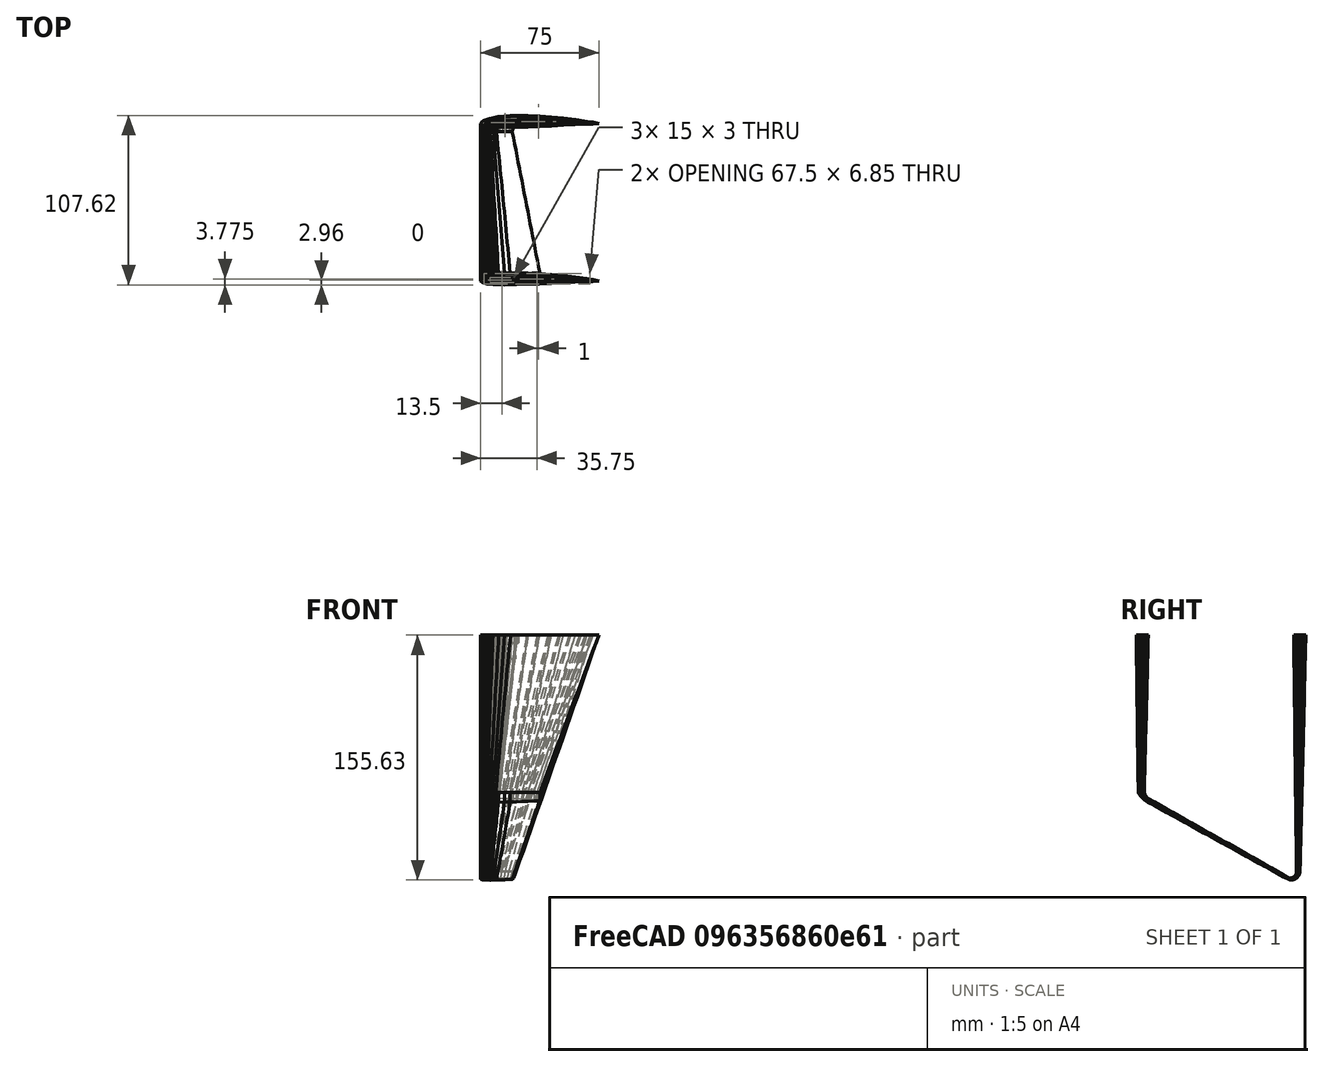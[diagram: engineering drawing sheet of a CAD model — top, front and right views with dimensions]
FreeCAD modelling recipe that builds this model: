
FCSTD DOCUMENT  (FreeCAD 0.16R6712 (Git))
Label: Aile_double_tribord_2
License: All rights reserved
LicenseURL: http://en.wikipedia.org/wiki/All_rights_reserved
objects: Part::FeaturePython×6, Part::Loft×5, Part::Part2DObjectPython×4, Sketcher::SketchObject×3, Part::Sweep×2, Part::Cut×2, PartDesign::Pad×2, Mesh::Feature×2, Part::MultiFuse×1
note: 27 computed .brp shape members not serialized (recipe doc carries the construction recipe); baked Part::Feature solids carry a one-line shape summary decoded from their .brp

FEATURE [Part::Part2DObjectPython] DWire  label="DWire_base"  # Draft 2D object (typed FeaturePython)
  ChamferSize = 0
  Closed = true
  End = (75,-0.07875,0)
  FilletRadius = 0
  Length = 152.352
  MakeFace = true
  Points = (35) [(75,0.07875,0),(71.2807,0.7425,0),(67.5502,1.362,0),(60.0727,2.472,0),(52.5765,3.41325,0),(45.0637,4.185,0),(37.5367,4.767,0),(30,5.12775,0),+27 more]
  Start = (75,0.07875,0)
  Subdivisions = 0
FEATURE [Part::FeaturePython] Scale  label="Scale_bout"  # Draft clone (typed FeaturePython)
  Objects = -> [DWire]
  Placement = pos=(0,0,-100) rot=(0,0,1;0rad)
  Scale = (0.5,0.5,1)
FEATURE [Part::FeaturePython] Scale001  label="Scale_int_base"  # Draft clone (typed FeaturePython)
  Objects = -> [DWire]
  Placement = pos=(2,0.1,0) rot=(0,0,1;0rad)
  Scale = (0.9,0.9,0.9)
FEATURE [Part::FeaturePython] Scale002  label="Scale_int_bout"  # Draft clone (typed FeaturePython)
  Objects = -> [Scale]
  Placement = pos=(3,0.2,-100) rot=(0,0,1;0rad)
  Scale = (0.7,0.7,1)
FEATURE [Part::Part2DObjectPython] DWire001  label="DWire_base_haut"  # Draft 2D object (typed FeaturePython)
  ChamferSize = 0
  Closed = true
  End = (75,99.9213,0)
  FilletRadius = 0
  Length = 152.352
  MakeFace = true
  Placement = pos=(0,100,0) rot=(0,0,1;0rad)
  Points = (35) [(75,0.07875,0),(71.2807,0.7425,0),(67.5502,1.362,0),(60.0727,2.472,0),(52.5765,3.41325,0),(45.0637,4.185,0),(37.5367,4.767,0),(30,5.12775,0),+27 more]
  Start = (75,100.079,0)
  Subdivisions = 0
FEATURE [Part::FeaturePython] Scale003  label="Scale_int_base_haut"  # Draft clone (typed FeaturePython)
  Objects = -> [DWire001]
  Placement = pos=(3,110.1,0) rot=(0,0,1;0rad)
  Scale = (0.9,0.9,1)
FEATURE [Part::FeaturePython] Scale004  label="Scale_bout_haut"  # Draft clone (typed FeaturePython)
  Objects = -> [DWire001]
  Placement = pos=(0,170,-150) rot=(0,0,1;0rad)
  Scale = (0.3,0.3,1)
FEATURE [Part::FeaturePython] Scale005  label="Scale_int_bout_haut"  # Draft clone (typed FeaturePython)
  Objects = -> [Scale004]
  Placement = pos=(3,220.2,-150) rot=(0,0,1;0rad)
  Scale = (0.5,0.5,1)
FEATURE [Part::Part2DObjectPython] DWire002  # Draft 2D object (typed FeaturePython)
  ChamferSize = 0
  Closed = true
  End = (37.5,5,-105.024)
  FilletRadius = 0
  Length = 75.448
  MakeFace = true
  Placement = pos=(0,5,-105) rot=(1,0,0;1.5708rad)
  Points = (35) [(37.5,0.023625,0),(35.625,0.151125,0),(33.75,0.2715,0),(30,0.492,0),(26.25,0.687,0),(22.5,0.85575,0),(18.75,0.992625,0),(15,1.08825,0),+27 more]
  Start = (37.5,5,-104.976)
  Subdivisions = 0
FEATURE [Part::Part2DObjectPython] DWire004  # Draft 2D object (typed FeaturePython)
  ChamferSize = 0
  Closed = true
  End = (20,95,-155.013)
  FilletRadius = 0
  Length = 40.2389
  MakeFace = true
  Placement = pos=(0,95,-155) rot=(1,0,0;1.5708rad)
  Points = (35) [(20,0.0126,0),(19,0.0806,0),(18,0.1448,0),(16,0.2624,0),(14,0.3664,0),(12,0.4564,0),(10,0.5294,0),(8,0.5804,0),(6,0.6002,0),(5,0.5942,0),(4,0.5738,0),+24 more]
  Start = (20,95,-154.987)
  Subdivisions = 0
FEATURE [Part::Loft] Loft
  Closed = false
  Ruled = false
  Sections = -> [Scale001,Scale002]
  Solid = true
FEATURE [Part::Loft] Loft001
  Closed = false
  Ruled = false
  Sections = -> [Scale,DWire]
  Solid = true
FEATURE [Part::Loft] Loft002
  Closed = false
  Ruled = false
  Sections = -> [Scale003,Scale005]
  Solid = true
FEATURE [Part::Loft] Loft003
  Closed = false
  Ruled = false
  Sections = -> [Scale004,DWire001]
  Solid = true
FEATURE [Part::Loft] Loft004
  Closed = false
  Ruled = false
  Sections = -> [DWire002,DWire004]
  Solid = true
FEATURE [Sketcher::SketchObject] Sketch
  Placement = pos=(0,0,0) rot=(0.57735,0.57735,0.57735;2.0944rad)
  sketch-geometry (6):
    g0: ArcOfCircle CenterX=95 CenterY=-150 CenterZ=0 NormalX=0 NormalY=0 NormalZ=1 Radius=5 StartAngle=4.71239 EndAngle=6.28319
    g1: LineSegment [constr] StartX=100 StartY=-150 StartZ=0 EndX=100 EndY=-157.887 EndZ=0
    g2: LineSegment [constr] StartX=95 StartY=-155 StartZ=0 EndX=100 EndY=-157.887 EndZ=0
    g3: LineSegment [constr] StartX=0 StartY=-100 StartZ=0 EndX=0 EndY=-110.771 EndZ=0
    g4: LineSegment [constr] StartX=5 StartY=-105 StartZ=0 EndX=0 EndY=-102.113 EndZ=0
    g5: ArcOfCircle CenterX=11.8301 CenterY=-93.1699 CenterZ=0 NormalX=0 NormalY=0 NormalZ=1 Radius=13.6602 StartAngle=3.66519 EndAngle=4.18879
  constraints (20):
    c: Vertical(g1)
    c: Coincident(g0,g1)
    c: Coincident(g0,g2)
    c: Coincident(g1,g2)
    c: Angle(g1,g2) = 1.0472
    c: Tangent(g1,g0,g0) = 1.5708
    c: DistanceY(g0,g-1) = 150
    c: DistanceX(g-1,g0) = 100
    c: DistanceY(g0,g0) = 5
    c: DistanceX(g0,g0) = 5
    c: Vertical(g3)
    c: PointOnObject(g3,g-2)
    c: DistanceY(g3,g-1) = 100
    c: Angle(g3,g4) = 1.0472
    c: Coincident(g5,g3)
    c: DistanceX(g3,g4) = 5
    c: Coincident(g5,g4)
    c: DistanceY(g4,g3) = 5
    c: PointOnObject(g4,g3)
    c: Tangent(g4,g5)
FEATURE [Part::Sweep] Sweep
  Frenet = false
  Sections = -> [Scale,DWire002]
  Solid = true
  Spine = -> Sketch [Edge2]
  Transition = 1
FEATURE [Part::Sweep] Sweep001
  Frenet = false
  Sections = -> [DWire004,Scale004]
  Solid = true
  Spine = -> Sketch [Edge1]
  Transition = 1
FEATURE [Part::Cut] Cut
  Base = -> Loft001
  Tool = -> Loft
FEATURE [Part::Cut] Cut001
  Base = -> Loft003
  Tool = -> Loft002
FEATURE [Part::MultiFuse] Fusion
  Shapes = -> [Sweep,Sweep001,Loft004,Cut,Cut001]
FEATURE [Sketcher::SketchObject] Sketch001
  ExternalGeometry = -> [Fusion]
  Support = -> Fusion [Face17]
  sketch-geometry (20):
    g0: LineSegment StartX=6 StartY=2 StartZ=0 EndX=21 EndY=2 EndZ=0
    g1: LineSegment StartX=21 StartY=2 StartZ=0 EndX=21 EndY=-1 EndZ=0
    g2: LineSegment StartX=21 StartY=-1 StartZ=0 EndX=6 EndY=-1 EndZ=0
    g3: LineSegment StartX=6 StartY=-1 StartZ=0 EndX=6 EndY=2 EndZ=0
    g4: LineSegment StartX=5 StartY=2.32561 StartZ=0 EndX=5 EndY=-1.45606 EndZ=0
    g5: LineSegment StartX=22 StartY=4.73385 StartZ=0 EndX=22 EndY=-2.01648 EndZ=0
    g6: LineSegment StartX=5 StartY=2.32561 StartZ=0 EndX=5.20085 EndY=2.4085 EndZ=0
    g7: LineSegment StartX=5.20085 StartY=2.4085 StartZ=0 EndX=6.87148 EndY=2.91407 EndZ=0
    g8: LineSegment StartX=6.87148 StartY=2.91407 StartZ=0 EndX=8.55425 EndY=3.31705 EndZ=0
    g9: LineSegment StartX=8.55425 StartY=3.31705 StartZ=0 EndX=11.9374 EndY=3.92387 EndZ=0
    g10: LineSegment StartX=11.9374 StartY=3.92387 StartZ=0 EndX=15.3387 EndY=4.3363 EndZ=0
    g11: LineSegment StartX=15.3387 StartY=4.3363 StartZ=0 EndX=18.7494 EndY=4.6009 EndZ=0
    g12: LineSegment StartX=18.7494 StartY=4.6009 StartZ=0 EndX=22 EndY=4.73385 EndZ=0
    g13: LineSegment StartX=22 StartY=-2.01648 StartZ=0 EndX=19.0006 EndY=-2.08025 EndZ=0
    g14: LineSegment StartX=19.0006 StartY=-2.08025 StartZ=0 EndX=15.6613 EndY=-2.1113 EndZ=0
    g15: LineSegment StartX=15.6613 StartY=-2.1113 StartZ=0 EndX=12.3126 EndY=-2.07823 EndZ=0
    g16: LineSegment StartX=12.3126 StartY=-2.07823 StartZ=0 EndX=8.94575 EndY=-1.9358 EndZ=0
    g17: LineSegment StartX=8.94575 StartY=-1.9358 StartZ=0 EndX=7.25352 EndY=-1.79608 EndZ=0
    g18: LineSegment StartX=7.25352 StartY=-1.79608 StartZ=0 EndX=5.54915 EndY=-1.57535 EndZ=0
    g19: LineSegment StartX=5.54915 StartY=-1.57535 StartZ=0 EndX=5 EndY=-1.45606 EndZ=0
  constraints (50):
    c: Coincident(g0,g1)
    c: Coincident(g1,g2)
    c: Coincident(g2,g3)
    c: Coincident(g3,g0)
    c: Horizontal(g0)
    c: Horizontal(g2)
    c: Vertical(g1)
    c: Vertical(g3)
    c: Vertical(g4)
    c: Vertical(g5)
    c: DistanceY(g3,g3) = 3
    c: DistanceX(g0,g0) = 15
    c: DistanceX(g4,g0) = 1
    c: DistanceX(g0,g5) = 1
    c: DistanceX(g-1,g2) = 6
    c: DistanceY(g2,g-1) = 1
    c: PointOnObject(g4,g-18)
    c: PointOnObject(g4,g-15)
    c: PointOnObject(g5,g-6)
    c: PointOnObject(g5,g-9)
    c: Coincident(g6,g4)
    c: Coincident(g6,g-18)
    c: Coincident(g7,g6)
    c: Coincident(g7,g-14)
    c: Coincident(g8,g7)
    c: Coincident(g8,g-14)
    c: Coincident(g9,g8)
    c: Coincident(g9,g-4)
    c: Coincident(g10,g-5)
    c: Coincident(g10,g9)
    c: Coincident(g11,g10)
    c: Coincident(g11,g-6)
    c: PointOnObject(g12,g-6)
    c: Coincident(g12,g5)
    c: Coincident(g11,g12)
    c: Coincident(g11,g-5)
    c: Coincident(g13,g5)
    c: Coincident(g13,g-10)
    c: Coincident(g14,g13)
    c: Coincident(g15,g14)
    c: Coincident(g15,g-12)
    c: Coincident(g14,g-11)
    c: Coincident(g16,g15)
    c: Coincident(g16,g-17)
    c: Coincident(g17,g16)
    c: Coincident(g17,g-17)
    c: Coincident(g18,g17)
    c: Coincident(g18,g-16)
    c: Coincident(g19,g18)
    c: Coincident(g19,g4)
FEATURE [PartDesign::Pad] Pad
  Length = 15
  Length2 = 100
  Reversed = true
  Sketch = -> Sketch001
  Type = 0
FEATURE [Sketcher::SketchObject] Sketch002
  ExternalGeometry = -> [Pad]
  Support = -> Pad [Face223]
  sketch-geometry (18):
    g0: LineSegment StartX=8 StartY=102 StartZ=0 EndX=23 EndY=102 EndZ=0
    g1: LineSegment StartX=23 StartY=102 StartZ=0 EndX=23 EndY=99 EndZ=0
    g2: LineSegment StartX=23 StartY=99 StartZ=0 EndX=8 EndY=99 EndZ=0
    g3: LineSegment StartX=8 StartY=99 StartZ=0 EndX=8 EndY=102 EndZ=0
    g4: LineSegment StartX=7 StartY=103.507 StartZ=0 EndX=7 EndY=97.7972 EndZ=0
    g5: LineSegment StartX=24 StartY=105.15 StartZ=0 EndX=24 EndY=97.6973 EndZ=0
    g6: LineSegment StartX=7 StartY=103.507 StartZ=0 EndX=7.2825 EndY=103.575 EndZ=0
    g7: LineSegment StartX=7.2825 StartY=103.575 StartZ=0 EndX=11.0415 EndY=104.249 EndZ=0
    g8: LineSegment StartX=11.0415 StartY=104.249 StartZ=0 EndX=14.8208 EndY=104.707 EndZ=0
    g9: LineSegment StartX=14.8208 StartY=104.707 StartZ=0 EndX=18.6105 EndY=105.001 EndZ=0
    g10: LineSegment StartX=18.6105 StartY=105.001 StartZ=0 EndX=22.4062 EndY=105.156 EndZ=0
    g11: LineSegment StartX=22.4062 StartY=105.156 StartZ=0 EndX=24 EndY=105.15 EndZ=0
    g12: LineSegment StartX=7 StartY=97.7972 StartZ=0 EndX=7.7175 EndY=97.738 EndZ=0
    g13: LineSegment StartX=7.7175 StartY=97.738 StartZ=0 EndX=11.4585 EndY=97.5798 EndZ=0
    g14: LineSegment StartX=11.4585 StartY=97.5798 StartZ=0 EndX=15.1792 EndY=97.543 EndZ=0
    g15: LineSegment StartX=15.1792 StartY=97.543 StartZ=0 EndX=18.8895 EndY=97.5775 EndZ=0
    g16: LineSegment StartX=18.8895 StartY=97.5775 StartZ=0 EndX=22.5938 EndY=97.6562 EndZ=0
    g17: LineSegment StartX=22.5938 StartY=97.6562 StartZ=0 EndX=24 EndY=97.6973 EndZ=0
  constraints (44):
    c: Coincident(g0,g1)
    c: Coincident(g1,g2)
    c: Coincident(g2,g3)
    c: Coincident(g3,g0)
    c: Horizontal(g0)
    c: Horizontal(g2)
    c: Vertical(g1)
    c: Vertical(g3)
    c: DistanceY(g3,g3) = 3
    c: DistanceX(g0,g0) = 15
    c: DistanceX(g-3,g2) = 8
    c: Vertical(g4)
    c: Vertical(g5)
    c: DistanceX(g1,g5) = 1
    c: DistanceX(g4,g2) = 1
    c: DistanceY(g2,g-3) = 1
    c: PointOnObject(g4,g-15)
    c: PointOnObject(g4,g-4)
    c: PointOnObject(g5,g-9)
    c: PointOnObject(g5,g-10)
    c: Coincident(g6,g4)
    c: Coincident(g6,g-5)
    c: Coincident(g7,g6)
    c: Coincident(g7,g-6)
    c: Coincident(g8,g7)
    c: Coincident(g8,g-7)
    c: Coincident(g9,g8)
    c: Coincident(g9,g-8)
    c: Coincident(g10,g9)
    c: Coincident(g10,g-9)
    c: Coincident(g11,g10)
    c: Coincident(g11,g5)
    c: Coincident(g12,g-15)
    c: Coincident(g13,g12)
    c: Coincident(g13,g-14)
    c: Coincident(g4,g12)
    c: Coincident(g14,g13)
    c: Coincident(g14,g-13)
    c: Coincident(g15,g-12)
    c: Coincident(g14,g15)
    c: Coincident(g16,g15)
    c: Coincident(g16,g-11)
    c: Coincident(g17,g16)
    c: Coincident(g17,g5)
FEATURE [PartDesign::Pad] Pad001
  Length = 5
  Length2 = 100
  Reversed = true
  Sketch = -> Sketch002
  Type = 0
FEATURE [Mesh::Feature] Aile_renfort_interne
  Placement = pos=(6,-1,-15) rot=(0,0,1;0rad)
FEATURE [Mesh::Feature] Aile_renfort_interne001
  Placement = pos=(8,99,-5) rot=(0,0,1;0rad)
